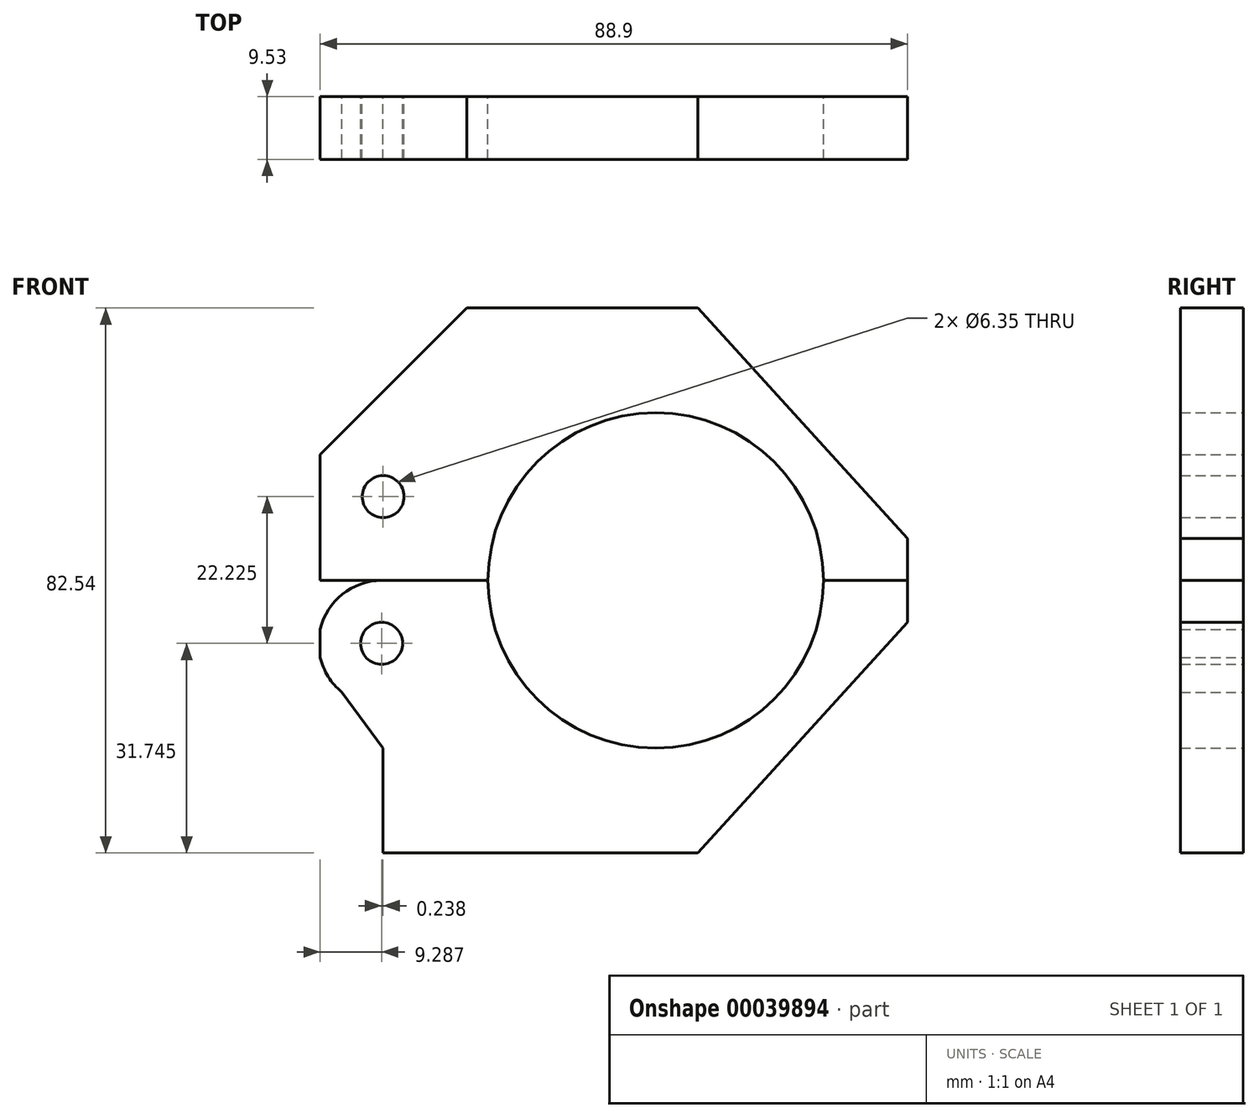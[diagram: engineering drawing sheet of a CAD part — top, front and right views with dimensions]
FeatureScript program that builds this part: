
annotation { "Feature Type Name" : "Feature", "Feature Type Description" : "" }
export const myFeature = defineFeature(function(context is Context, id is Id, definition is map)
    precondition{}
    {
        {
            var Q0;
            Q0=qCreatedBy(makeId("Front.planeOp"),FACE);
            var sketch = newSketch(context, id + "F0", { "sketchPlane" : qUnion([Q0])});
            skLineSegment(sketch, "E0.rect.bottom", {"start": v(-22.23, 41.28) * mm, "end": v(12.7, 41.28) * mm});
            skLineSegment(sketch, "E0.rect.top", {"start": v(-34.93, -41.28) * mm, "end": v(12.7, -41.28) * mm});
            skLineSegment(sketch, "E0.rect.left", {"start": v(-44.45, 19.05) * mm, "end": v(-44.45, 0) * mm});
            skLineSegment(sketch, "E0.rect.right", {"start": v(44.45, 6.35) * mm, "end": v(44.45, -6.35) * mm});
            skPoint(sketch, "E0.rect.middle", {"position": v(0, 0) * mm});
            skLineSegment(sketch, "E1", {"start": v(0, 0) * mm, "end": v(44.45, 0) * mm});
            skLineSegment(sketch, "E2", {"start": v(44.45, 0) * mm, "end": v(-44.45, 0) * mm});
            skCircle(sketch, "E3", {"center": v(6.35, 0) * mm, "radius": 25.4 * mm});
            skLineSegment(sketch, "E4", {"start": v(12.7, 41.27) * mm, "end": v(44.45, 6.35) * mm});
            skLineSegment(sketch, "E5.MirrorCS", {"start": v(12.7, -41.27) * mm, "end": v(44.45, -6.35) * mm});
            skLineSegment(sketch, "E6", {"start": v(-22.23, 41.27) * mm, "end": v(-44.45, 19.05) * mm});
            skCircle(sketch, "E7", {"center": v(-34.93, 12.7) * mm, "radius": 3.18 * mm});
            skLineSegment(sketch, "E8", {"start": v(-34.93, -41.28) * mm, "end": v(-34.93, -25.4) * mm});
            skCircle(sketch, "E9", {"center": v(-35.16, -9.53) * mm, "radius": 3.18 * mm});
            skArc(sketch, "E10", {"start": v(-35.16, 0) * mm, "mid": v(-44.14, -6.34) * mm, "end": v(-41.16, -16.93) * mm});
            skLineSegment(sketch, "E11", {"start": v(-34.93, -25.4) * mm, "end": v(-41.16, -16.93) * mm});
            skPoint(sketch, "E12.orphan", {"position": v(44.45, 41.28) * mm});
            skPoint(sketch, "E13.orphan", {"position": v(44.45, -41.28) * mm});
            skLineSegment(sketch, "E14.trimOffspring", {"start": v(-44.45, -7.41) * mm, "end": v(-44.45, -11.64) * mm});
            skPoint(sketch, "E15.orphan", {"position": v(-44.45, -41.28) * mm});
            skPoint(sketch, "E16.orphan", {"position": v(-44.45, 41.28) * mm});
            skSolve(sketch);
        }
        {
            var Q0;
            Q0=makeQuery(id+"F0.imprint","IMPRINT",FACE,{"disambiguationData":[TD([[makeQuery(id+"F0.imprint","IMPRINT",EDGE,{"derivedFrom":sQuery(id+"F0.wireOp",EDGE,"E0.rect.bottom")}),-1.0]])]});
            extrude(context, id + "F1", {"entities" : qUnion([Q0]), "depth" : 9.52 * mm});
        }
        {
            var Q0;
            Q0=makeQuery(id+"F0.imprint","IMPRINT",FACE,{"disambiguationData":[TD([[makeQuery(id+"F0.imprint","IMPRINT",EDGE,{"derivedFrom":sQuery(id+"F0.wireOp",EDGE,"E0.rect.top")}),1.0]])]});
            extrude(context, id + "F2", {"entities" : qUnion([Q0]), "depth" : 9.52 * mm});
        }
    });
